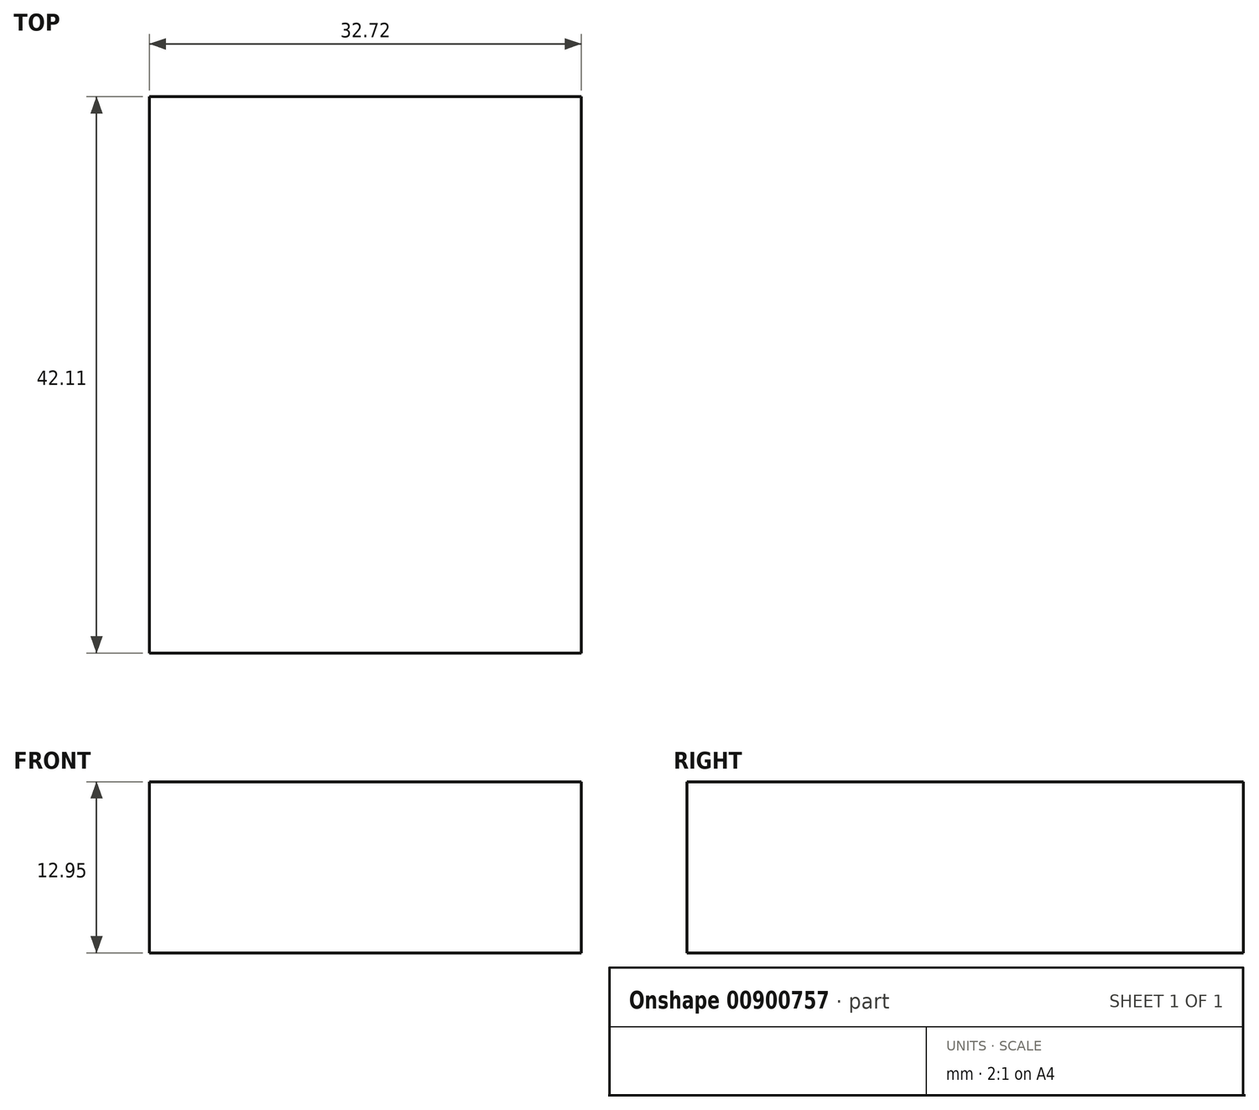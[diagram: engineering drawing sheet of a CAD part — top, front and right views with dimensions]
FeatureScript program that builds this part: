
annotation { "Feature Type Name" : "Feature", "Feature Type Description" : "" }
export const myFeature = defineFeature(function(context is Context, id is Id, definition is map)
    precondition{}
    {
        {
            var Q0;
            Q0=qCreatedBy(makeId("Top.planeOp"),FACE);
            var sketch = newSketch(context, id + "F0", { "sketchPlane" : qUnion([Q0])});
            skLineSegment(sketch, "E0.bottom", {"start": v(0, 0) * mm, "end": v(32.72, 0) * mm});
            skLineSegment(sketch, "E0.top", {"start": v(0, -42.11) * mm, "end": v(32.72, -42.11) * mm});
            skLineSegment(sketch, "E0.left", {"start": v(0, 0) * mm, "end": v(0, -42.11) * mm});
            skLineSegment(sketch, "E0.right", {"start": v(32.72, 0) * mm, "end": v(32.72, -42.11) * mm});
            skSolve(sketch);
        }
        {
            var Q0;
            Q0=makeQuery(id+"F0.imprint","IMPRINT",FACE,{"disambiguationData":[TD([[makeQuery(id+"F0.imprint","IMPRINT",EDGE,{"derivedFrom":sQuery(id+"F0.wireOp",EDGE,"E0.bottom")}),-1.0]])]});
            extrude(context, id + "F1", {"entities" : qUnion([Q0]), "depth" : 12.95 * mm, "offsetDistance" : 25.4 * mm});
        }
    });
